# Revit family: Accessory-Robe_Hook-KOHLER-LOURE-K-11587T
name_source: partatom
category: Specialty Equipment
revit_build: Autodesk Revit 2017 (Build: 20160225_1515(x64)
units: mm (PartAtom-declared; Revit-internal decimal feet)

## family parameters
Cut with Voids When Loaded = No
Host = Face
OmniClass Number = 23.31.25.25
OmniClass Title = Towel Bars
Part Type = Normal
Room Calculation Point = No
Round Connector Dimension = Use Diameter
Shared = No

## types (1)
- CP-Polished Chrome
    ADA Compliant = No
    Assembly Code = C1030200
    Date Modified = 06/07/2020
    Default Elevation = 42"
    Description = Towel Ring
    Finish = Kohler-Metal-CP-Polished_Chrome
    Height = 3 3/4"
    Length = 2 3/4"
    Manufacturer = KOHLER Co.
    Master Format 2014 = 10 28 00
    Master Format 2014 Name = Toilet, Bath, and Laundry Accessories
    Material = Premium Metal Construction
    Model = K-11587T-CP
    Product Documentation Link = https://files.kohler.com.cn
    Product Name = LOURE
    Product Page URL = https://www.kohler.com.cn
    URL = http://www.kohler.com.cn
    WaterSense Certified = No
    Width = 12"

## geometry (parser evidence)
native form markers: Sweep x5
no freeform markers — native parametric forms only
